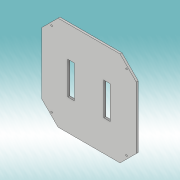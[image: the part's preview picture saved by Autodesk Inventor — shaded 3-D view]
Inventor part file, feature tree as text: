
AUTODESK INVENTOR PART (.ipt)
format: ipt  version: 2019 (Build 230136000, 136)  size: 131,072 bytes
history: native  units: mm
features: extrude x3, sketch x3
ambient origin geometry x8: Origin, YZ Plane, XZ Plane, XY Plane, X Axis, Y Axis, Z Axis, Center Point
bodies: Solid1 (feature_tree)
feature tree (6):
  extrude  "Extrusion1"  Depth=47.5mm
  extrude  "Extrusion2"  Depth=3.0mm TaperAngle=0.0deg
  extrude  "Extrusion3"  Depth=10.0mm
  sketch  "Sketch1"  dims[d0=47.5mm d2=35.0mm]
  sketch  "Sketch2"  dims[d3=135.0deg d4=3.0mm d5=0.0mm]
  sketch  "Sketch3"  dims[d6=50.0mm d7=10.0mm d8=45.0mm d10=47.5mm d11=3.0mm d12=0.0mm d13=2.5mm d14=3.5mm d15=0.1mm d16=0.0mm]
